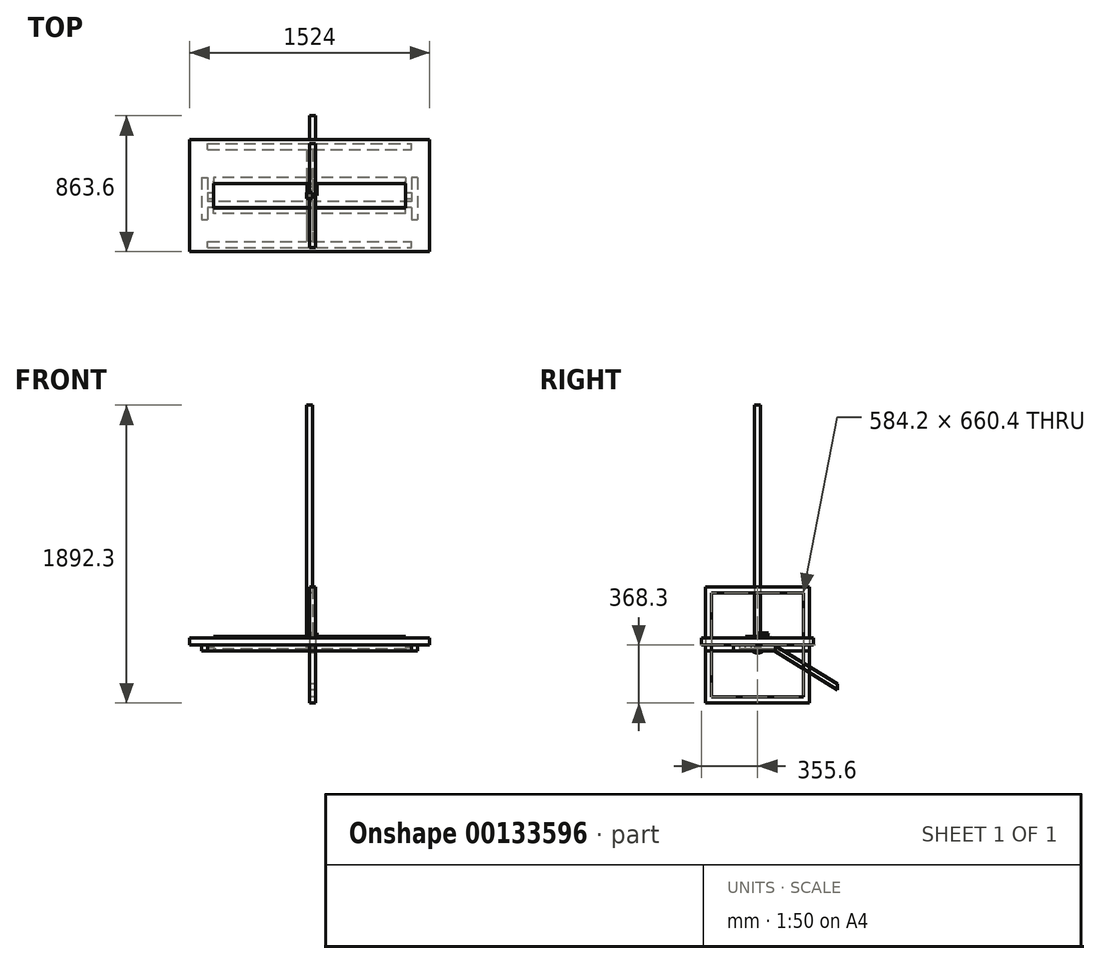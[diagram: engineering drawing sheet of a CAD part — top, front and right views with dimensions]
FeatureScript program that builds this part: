
annotation { "Feature Type Name" : "Feature", "Feature Type Description" : "" }
export const myFeature = defineFeature(function(context is Context, id is Id, definition is map)
    precondition{}
    {
        {
            var Q0;
            Q0=qCreatedBy(makeId("Top.planeOp"),FACE);
            var sketch = newSketch(context, id + "F0", { "sketchPlane" : qUnion([Q0])});
            skLineSegment(sketch, "E0.bottom", {"start": v(762, 355.6) * mm, "end": v(-762, 355.6) * mm});
            skLineSegment(sketch, "E0.top", {"start": v(762, -355.6) * mm, "end": v(-762, -355.6) * mm});
            skLineSegment(sketch, "E0.left", {"start": v(762, 355.6) * mm, "end": v(762, -355.6) * mm});
            skLineSegment(sketch, "E0.right", {"start": v(-762, 355.6) * mm, "end": v(-762, -355.6) * mm});
            skPoint(sketch, "E0.middle", {"position": v(0, 0) * mm});
            skSolve(sketch);
        }
        {
            var Q0;
            Q0=makeQuery(id+"F0.imprint","IMPRINT",FACE,{"disambiguationData":[TD([[makeQuery(id+"F0.imprint","IMPRINT",EDGE,{"derivedFrom":sQuery(id+"F0.wireOp",EDGE,"E0.bottom")}),1.0]])]});
            extrude(context, id + "F1", {"entities" : qUnion([Q0]), "depth" : 44.45 * mm});
        }
        {
            var Q0;
            Q0=makeQuery(id+"F1.opExtrude","CAP_FACE",FACE,{"disambiguationData":[OSD([sQuery(id+"F0.wireOp",EDGE,"E0.bottom"),sQuery(id+"F0.wireOp",EDGE,"E0.top"),sQuery(id+"F0.wireOp",EDGE,"E0.left"),sQuery(id+"F0.wireOp",EDGE,"E0.right")])],"isStart":true});
            var sketch = newSketch(context, id + "F2", { "sketchPlane" : qUnion([Q0])});
            skLineSegment(sketch, "E1.bottom", {"start": v(19.05, -292.1) * mm, "end": v(-19.05, -292.1) * mm});
            skLineSegment(sketch, "E1.top", {"start": v(19.05, 292.1) * mm, "end": v(-19.05, 292.1) * mm});
            skLineSegment(sketch, "E1.left", {"start": v(19.05, -292.1) * mm, "end": v(19.05, 292.1) * mm});
            skLineSegment(sketch, "E1.right", {"start": v(-19.05, -292.1) * mm, "end": v(-19.05, 292.1) * mm});
            skPoint(sketch, "E1.middle", {"position": v(0, 0) * mm});
            skLineSegment(sketch, "E2", {"start": v(0, 0) * mm, "end": v(0, 311.15) * mm, "construction": true});
            skPoint(sketch, "E2.endSnap0", {"position": v(0, 292.1) * mm});
            skLineSegment(sketch, "E3", {"start": v(0, 0) * mm, "end": v(0, -311.15) * mm, "construction": true});
            skLineSegment(sketch, "E4.bottom", {"start": v(-647.7, 330.2) * mm, "end": v(647.7, 330.2) * mm});
            skLineSegment(sketch, "E4.top", {"start": v(-647.7, 292.1) * mm, "end": v(647.7, 292.1) * mm});
            skLineSegment(sketch, "E4.left", {"start": v(-647.7, 330.2) * mm, "end": v(-647.7, 292.1) * mm});
            skLineSegment(sketch, "E4.right", {"start": v(647.7, 330.2) * mm, "end": v(647.7, 292.1) * mm});
            skPoint(sketch, "E4.middle", {"position": v(0, 311.15) * mm});
            skLineSegment(sketch, "E5.bottom", {"start": v(-647.7, -292.1) * mm, "end": v(647.7, -292.1) * mm});
            skLineSegment(sketch, "E5.top", {"start": v(-647.7, -330.2) * mm, "end": v(647.7, -330.2) * mm});
            skLineSegment(sketch, "E5.left", {"start": v(-647.7, -292.1) * mm, "end": v(-647.7, -330.2) * mm});
            skLineSegment(sketch, "E5.right", {"start": v(647.7, -292.1) * mm, "end": v(647.7, -330.2) * mm});
            skPoint(sketch, "E5.middle", {"position": v(0, -311.15) * mm});
            skSolve(sketch);
        }
        {
            var Q0;
            {var subQ0=sQuery(id+"F2.wireOp",EDGE,"E1.left");Q0=makeQuery(id+"F2.imprint","IMPRINT",FACE,{"disambiguationData":[TD([[makeQuery(id+"F2.imprint","IMPRINT",EDGE,{"derivedFrom":subQ0}),1.0]])]});}
            var Q1;
            Q1=makeQuery(id+"F2.imprint","IMPRINT",FACE,{"disambiguationData":[TD([[makeQuery(id+"F2.imprint","IMPRINT",EDGE,{"derivedFrom":sQuery(id+"F2.wireOp",EDGE,"E5.top")}),1.0]])]});
            var Q2;
            Q2=makeQuery(id+"F2.imprint","IMPRINT",FACE,{"disambiguationData":[TD([[makeQuery(id+"F2.imprint","IMPRINT",EDGE,{"derivedFrom":sQuery(id+"F2.wireOp",EDGE,"E4.bottom")}),-1.0]])]});
            extrude(context, id + "F3", {"entities" : qUnion([Q0, Q1, Q2]), "depth" : 38.1 * mm});
        }
        {
            var Q0;
            Q0=qCreatedBy(makeId("Right.planeOp"),FACE);
            var sketch = newSketch(context, id + "F4", { "sketchPlane" : qUnion([Q0])});
            skLineSegment(sketch, "E6.bottom", {"start": v(-330.2, 368.3) * mm, "end": v(330.2, 368.3) * mm});
            skLineSegment(sketch, "E6.top", {"start": v(-330.2, -368.3) * mm, "end": v(330.2, -368.3) * mm});
            skLineSegment(sketch, "E6.left", {"start": v(-330.2, 368.3) * mm, "end": v(-330.2, -368.3) * mm});
            skLineSegment(sketch, "E6.right", {"start": v(330.2, 368.3) * mm, "end": v(330.2, -368.3) * mm});
            skPoint(sketch, "E6.middle", {"position": v(0, 0) * mm});
            skLineSegment(sketch, "E7.0", {"start": v(-292.1, 330.2) * mm, "end": v(292.1, 330.2) * mm});
            skLineSegment(sketch, "E7.1", {"start": v(-292.1, 330.2) * mm, "end": v(-292.1, -330.2) * mm});
            skLineSegment(sketch, "E7.2", {"start": v(-292.1, -330.2) * mm, "end": v(292.1, -330.2) * mm});
            skLineSegment(sketch, "E7.3", {"start": v(292.1, 330.2) * mm, "end": v(292.1, -330.2) * mm});
            skSolve(sketch);
        }
        {
            var Q0;
            Q0=makeQuery(id+"F4.imprint","IMPRINT",FACE,{"disambiguationData":[TD([[makeQuery(id+"F4.imprint","IMPRINT",EDGE,{"derivedFrom":sQuery(id+"F4.wireOp",EDGE,"E6.bottom")}),-1.0]])]});
            extrude(context, id + "F5", {"entities" : qUnion([Q0]), "depth" : 38.1 * mm});
        }
        {
            var Q0;
            Q0=qCreatedBy(makeId("Right.planeOp"),FACE);
            var sketch = newSketch(context, id + "F6", { "sketchPlane" : qUnion([Q0])});
            skLineSegment(sketch, "E8.bottom", {"start": v(19.05, 19.05) * mm, "end": v(-19.05, 19.05) * mm});
            skLineSegment(sketch, "E8.top", {"start": v(19.05, -19.05) * mm, "end": v(-19.05, -19.05) * mm});
            skLineSegment(sketch, "E8.left", {"start": v(19.05, 19.05) * mm, "end": v(19.05, -19.05) * mm});
            skLineSegment(sketch, "E8.right", {"start": v(-19.05, 19.05) * mm, "end": v(-19.05, -19.05) * mm});
            skPoint(sketch, "E8.middle", {"position": v(0, 0) * mm});
            skSolve(sketch);
        }
        {
            var Q0;
            Q0=makeQuery(id+"F6.imprint","IMPRINT",FACE,{"disambiguationData":[TD([[makeQuery(id+"F6.imprint","IMPRINT",EDGE,{"derivedFrom":sQuery(id+"F6.wireOp",EDGE,"E8.bottom")}),1.0]])]});
            extrude(context, id + "F7", {"entities" : qUnion([Q0]), "depth" : 1295.4 * mm, "symmetric" : true});
        }
        {
            var Q0;
            Q0=qCreatedBy(makeId("Top.planeOp"),FACE);
            var sketch = newSketch(context, id + "F8", { "sketchPlane" : qUnion([Q0])});
            skLineSegment(sketch, "E9.bottom", {"start": v(19.05, 19.05) * mm, "end": v(-19.05, 19.05) * mm});
            skLineSegment(sketch, "E9.top", {"start": v(19.05, -19.05) * mm, "end": v(-19.05, -19.05) * mm});
            skLineSegment(sketch, "E9.left", {"start": v(19.05, 19.05) * mm, "end": v(19.05, -19.05) * mm});
            skLineSegment(sketch, "E9.right", {"start": v(-19.05, 19.05) * mm, "end": v(-19.05, -19.05) * mm});
            skPoint(sketch, "E9.middle", {"position": v(0, 0) * mm});
            skSolve(sketch);
        }
        {
            var Q0;
            Q0=makeQuery(id+"F8.imprint","IMPRINT",FACE,{"disambiguationData":[TD([[makeQuery(id+"F8.imprint","IMPRINT",EDGE,{"derivedFrom":sQuery(id+"F8.wireOp",EDGE,"E9.bottom")}),1.0]])]});
            extrude(context, id + "F9", {"entities" : qUnion([Q0]), "depth" : 1524 * mm});
        }
        {
            var Q0;
            Q0=qCreatedBy(makeId("Top.planeOp"),FACE);
            var sketch = newSketch(context, id + "F10", { "sketchPlane" : qUnion([Q0])});
            skLineSegment(sketch, "E10.bottom", {"start": v(-762, 152.4) * mm, "end": v(762, 152.4) * mm});
            skLineSegment(sketch, "E10.top", {"start": v(-762, -152.4) * mm, "end": v(762, -152.4) * mm});
            skLineSegment(sketch, "E10.left", {"start": v(-762, 152.4) * mm, "end": v(-762, -152.4) * mm});
            skLineSegment(sketch, "E10.right", {"start": v(762, 152.4) * mm, "end": v(762, -152.4) * mm});
            skPoint(sketch, "E10.middle", {"position": v(0, 0) * mm});
            skSolve(sketch);
        }
        {
            var Q0;
            Q0=makeQuery(id+"F10.imprint","IMPRINT",FACE,{"disambiguationData":[TD([[makeQuery(id+"F10.imprint","IMPRINT",EDGE,{"derivedFrom":sQuery(id+"F10.wireOp",EDGE,"E10.bottom")}),-1.0]])]});
            extrude(context, id + "F11", {"entities" : qUnion([Q0]), "depth" : 28.57 * mm});
        }
        {
            var Q0;
            Q0=makeQuery(id+"F11.opExtrude","CAP_FACE",FACE,{"disambiguationData":[OSD([sQuery(id+"F10.wireOp",EDGE,"E10.bottom"),sQuery(id+"F10.wireOp",EDGE,"E10.top"),sQuery(id+"F10.wireOp",EDGE,"E10.left"),sQuery(id+"F10.wireOp",EDGE,"E10.right")])],"isStart":true});
            var sketch = newSketch(context, id + "F12", { "sketchPlane" : qUnion([Q0])});
            skLineSegment(sketch, "E11.bottom", {"start": v(647.7, 76.2) * mm, "end": v(-647.7, 76.2) * mm});
            skLineSegment(sketch, "E11.top", {"start": v(647.7, 38.1) * mm, "end": v(-647.7, 38.1) * mm});
            skLineSegment(sketch, "E11.left", {"start": v(647.7, 76.2) * mm, "end": v(647.7, 38.1) * mm});
            skLineSegment(sketch, "E11.right", {"start": v(-647.7, 76.2) * mm, "end": v(-647.7, 38.1) * mm});
            skPoint(sketch, "E11.middle", {"position": v(0, 0) * mm});
            skLineSegment(sketch, "E12", {"start": v(-685.8, -114.3) * mm, "end": v(-685.8, 152.4) * mm});
            skLineSegment(sketch, "E13", {"start": v(-647.7, 76.2) * mm, "end": v(-647.7, 152.4) * mm});
            skLineSegment(sketch, "E14", {"start": v(-685.8, 152.4) * mm, "end": v(-647.7, 152.4) * mm});
            skLineSegment(sketch, "E15", {"start": v(-685.8, -114.3) * mm, "end": v(-647.7, -114.3) * mm});
            skLineSegment(sketch, "E16", {"start": v(-647.7, -114.3) * mm, "end": v(-647.7, 38.1) * mm});
            skLineSegment(sketch, "E17.MirrorCS", {"start": v(647.7, 76.2) * mm, "end": v(647.7, 152.4) * mm});
            skLineSegment(sketch, "E18.MirrorCS", {"start": v(685.8, 152.4) * mm, "end": v(647.7, 152.4) * mm});
            skLineSegment(sketch, "E19.MirrorCS", {"start": v(685.8, -114.3) * mm, "end": v(685.8, 152.4) * mm});
            skLineSegment(sketch, "E20.MirrorCS", {"start": v(647.7, -114.3) * mm, "end": v(647.7, 38.1) * mm});
            skLineSegment(sketch, "E21.MirrorCS", {"start": v(685.8, -114.3) * mm, "end": v(647.7, -114.3) * mm});
            skLineSegment(sketch, "E22", {"start": v(0, 38.1) * mm, "end": v(0, -152.4) * mm, "construction": true});
            skSolve(sketch);
        }
        {
            var Q0;
            Q0=makeQuery(id+"F12.imprint","IMPRINT",FACE,{"disambiguationData":[TD([[makeQuery(id+"F12.imprint","IMPRINT",EDGE,{"derivedFrom":sQuery(id+"F12.wireOp",EDGE,"E11.right")}),-1.0]])]});
            var Q1;
            Q1=makeQuery(id+"F12.imprint","IMPRINT",FACE,{"disambiguationData":[TD([[makeQuery(id+"F12.imprint","IMPRINT",EDGE,{"derivedFrom":sQuery(id+"F12.wireOp",EDGE,"E11.left")}),1.0]])]});
            var Q2;
            Q2=makeQuery(id+"F12.imprint","IMPRINT",FACE,{"disambiguationData":[TD([[makeQuery(id+"F12.imprint","IMPRINT",EDGE,{"derivedFrom":sQuery(id+"F12.wireOp",EDGE,"E11.bottom")}),1.0]])]});
            extrude(context, id + "F13", {"entities" : qUnion([Q0, Q1, Q2]), "depth" : 38.1 * mm});
        }
        {
            var Q0;
            Q0=qCreatedBy(makeId("Right.planeOp"),FACE);
            var sketch = newSketch(context, id + "F14", { "sketchPlane" : qUnion([Q0])});
            skLineSegment(sketch, "E23.bottom", {"start": v(-76.2, 19.05) * mm, "end": v(76.2, 19.05) * mm});
            skLineSegment(sketch, "E23.top", {"start": v(-76.2, -19.05) * mm, "end": v(76.2, -19.05) * mm});
            skLineSegment(sketch, "E23.left", {"start": v(-76.2, 19.05) * mm, "end": v(-76.2, -19.05) * mm});
            skPoint(sketch, "E23.middle", {"position": v(0, 0) * mm});
            skLineSegment(sketch, "E24", {"start": v(-76.2, 19.05) * mm, "end": v(-76.2, -285.75) * mm, "construction": true});
            skLineSegment(sketch, "E25", {"start": v(-76.2, -285.75) * mm, "end": v(508, -285.75) * mm, "construction": true});
            skLineSegment(sketch, "E26", {"start": v(508, -285.75) * mm, "end": v(508, -247.65) * mm});
            skLineSegment(sketch, "E27", {"start": v(76.2, 19.05) * mm, "end": v(508, -247.65) * mm});
            skLineSegment(sketch, "E28", {"start": v(508, -285.75) * mm, "end": v(76.2, -19.05) * mm});
            skSolve(sketch);
        }
        {
            var Q0;
            Q0=makeQuery(id+"F14.imprint","IMPRINT",FACE,{"disambiguationData":[TD([[makeQuery(id+"F14.imprint","IMPRINT",EDGE,{"derivedFrom":sQuery(id+"F14.wireOp",EDGE,"E23.bottom")}),-1.0]])]});
            extrude(context, id + "F15", {"entities" : qUnion([Q0]), "depth" : 38.1 * mm});
        }
        {
            var Q0;
            Q0=qCreatedBy(makeId("Right.planeOp"),FACE);
            var sketch = newSketch(context, id + "F16", { "sketchPlane" : qUnion([Q0])});
            skLineSegment(sketch, "E29.bottom", {"start": v(12.7, 12.7) * mm, "end": v(-12.7, 12.7) * mm});
            skLineSegment(sketch, "E29.top", {"start": v(12.7, -12.7) * mm, "end": v(-12.7, -12.7) * mm});
            skLineSegment(sketch, "E29.left", {"start": v(12.7, 12.7) * mm, "end": v(12.7, -12.7) * mm});
            skLineSegment(sketch, "E29.right", {"start": v(-12.7, 12.7) * mm, "end": v(-12.7, -12.7) * mm});
            skPoint(sketch, "E29.middle", {"position": v(0, 0) * mm});
            skSolve(sketch);
        }
        {
            var Q0;
            Q0=makeQuery(id+"F16.imprint","IMPRINT",FACE,{"disambiguationData":[TD([[makeQuery(id+"F16.imprint","IMPRINT",EDGE,{"derivedFrom":sQuery(id+"F16.wireOp",EDGE,"E29.bottom")}),1.0]])]});
            extrude(context, id + "F17", {"entities" : qUnion([Q0]), "depth" : 1295.4 * mm, "symmetric" : true});
        }
        {
            var Q0;
            Q0=qCreatedBy(makeId("Right.planeOp"),FACE);
            var sketch = newSketch(context, id + "F18", { "sketchPlane" : qUnion([Q0])});
            skLineSegment(sketch, "E30.bottom", {"start": v(114.3, 25.4) * mm, "end": v(82.55, 25.4) * mm});
            skLineSegment(sketch, "E30.top", {"start": v(114.3, -25.4) * mm, "end": v(-114.3, -25.4) * mm});
            skLineSegment(sketch, "E30.left", {"start": v(114.3, 25.4) * mm, "end": v(114.3, -25.4) * mm});
            skLineSegment(sketch, "E30.right", {"start": v(-114.3, 25.4) * mm, "end": v(-114.3, -25.4) * mm});
            skPoint(sketch, "E30.middle", {"position": v(0, 0) * mm});
            skLineSegment(sketch, "E31", {"start": v(-82.55, 25.4) * mm, "end": v(-114.3, 25.4) * mm});
            skLineSegment(sketch, "E32", {"start": v(82.55, 25.4) * mm, "end": v(-82.55, 25.4) * mm, "construction": true});
            skLineSegment(sketch, "E33", {"start": v(0, 25.4) * mm, "end": v(0, 53.98) * mm, "construction": true});
            skPoint(sketch, "E33.endSnap0", {"position": v(0, 25.4) * mm});
            skLineSegment(sketch, "E34", {"start": v(0, 53.98) * mm, "end": v(76.2, 53.98) * mm});
            skLineSegment(sketch, "E35", {"start": v(0, 53.98) * mm, "end": v(-76.2, 53.98) * mm});
            skLineSegment(sketch, "E36", {"start": v(-82.55, 25.4) * mm, "end": v(-76.2, 53.98) * mm});
            skLineSegment(sketch, "E37", {"start": v(76.2, 53.98) * mm, "end": v(82.55, 25.4) * mm});
            skSolve(sketch);
        }
        {
            var Q0;
            Q0=makeQuery(id+"F18.imprint","IMPRINT",FACE,{"disambiguationData":[TD([[makeQuery(id+"F18.imprint","IMPRINT",EDGE,{"derivedFrom":sQuery(id+"F18.wireOp",EDGE,"E30.bottom")}),1.0]])]});
            extrude(context, id + "F19", {"entities" : qUnion([Q0]), "depth" : 1219.2 * mm, "symmetric" : true});
        }
        {
            var Q0;
            Q0=qCreatedBy(makeId("Right.planeOp"),FACE);
            var sketch = newSketch(context, id + "F20", { "sketchPlane" : qUnion([Q0])});
            skCircle(sketch, "E38", {"center": v(0, 0) * mm, "radius": 50.8 * mm});
            skSolve(sketch);
        }
        {
            var Q0;
            Q0=makeQuery(id+"F20.imprint","IMPRINT",FACE,{"disambiguationData":[TD([[makeQuery(id+"F20.imprint","IMPRINT",EDGE,{"derivedFrom":sQuery(id+"F20.wireOp",EDGE,"E38")}),1.0]])]});
            extrude(context, id + "F21", {"entities" : qUnion([Q0]), "depth" : 31.75 * mm});
        }
        {
            var Q0;
            Q0=qCreatedBy(makeId("Right.planeOp"),FACE);
            var sketch = newSketch(context, id + "F22", { "sketchPlane" : qUnion([Q0])});
            skLineSegment(sketch, "E39", {"start": v(0, 0) * mm, "end": v(0, 76.2) * mm, "construction": true});
            skLineSegment(sketch, "E40", {"start": v(38.1, 76.2) * mm, "end": v(69.85, 76.2) * mm});
            skLineSegment(sketch, "E41", {"start": v(38.1, 76.2) * mm, "end": v(6.35, 76.2) * mm});
            skLineSegment(sketch, "E42", {"start": v(38.1, 76.2) * mm, "end": v(0, 76.2) * mm, "construction": true});
            skArc(sketch, "E43", {"start": v(-12.3, 3.14) * mm, "mid": v(-5.34, -11.52) * mm, "end": v(10.35, -7.37) * mm});
            skLineSegment(sketch, "E44", {"start": v(6.35, 76.2) * mm, "end": v(-12.3, 3.14) * mm});
            skLineSegment(sketch, "E45", {"start": v(69.85, 76.2) * mm, "end": v(10.35, -7.37) * mm});
            skSolve(sketch);
        }
        {
            var Q0;
            Q0=makeQuery(id+"F22.imprint","IMPRINT",FACE,{"disambiguationData":[TD([[makeQuery(id+"F22.imprint","IMPRINT",EDGE,{"derivedFrom":sQuery(id+"F22.wireOp",EDGE,"E40")}),-1.0]])]});
            extrude(context, id + "F23", {"entities" : qUnion([Q0]), "operationType" : NewBodyOperationType.ADD, "depth" : 47.62 * mm, "hasSecondDirection" : true, "secondDirectionOppositeDirection" : true, "secondDirectionDepth" : 15.88 * mm});
        }
    });
